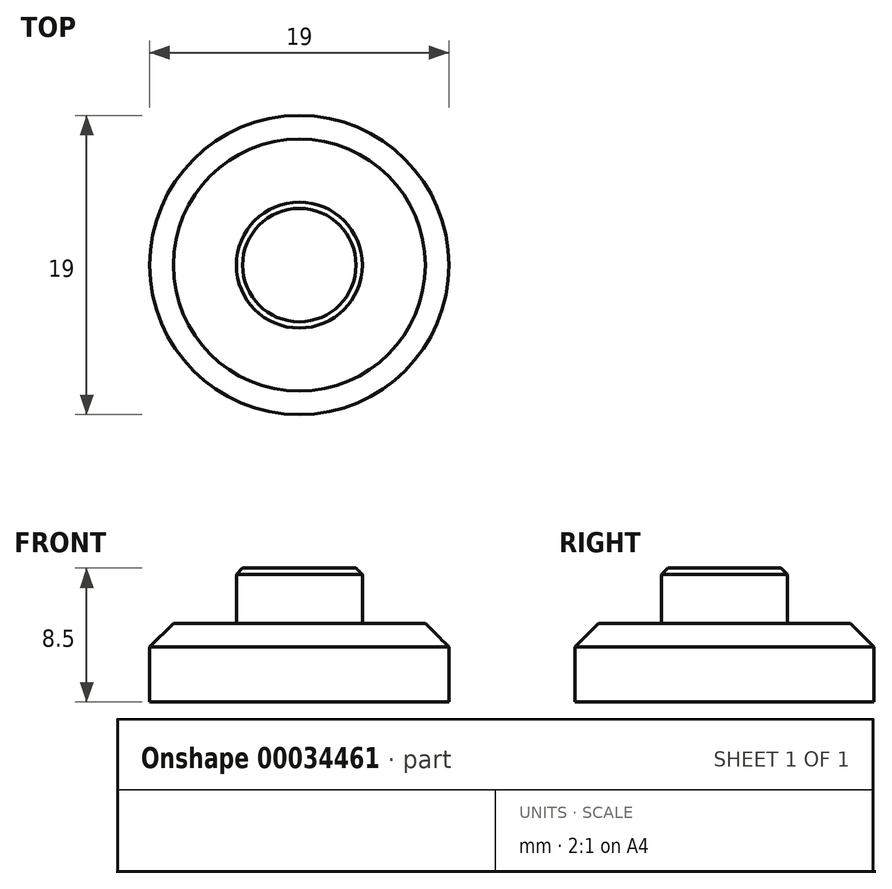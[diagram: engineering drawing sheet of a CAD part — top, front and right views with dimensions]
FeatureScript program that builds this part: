
annotation { "Feature Type Name" : "Feature", "Feature Type Description" : "" }
export const myFeature = defineFeature(function(context is Context, id is Id, definition is map)
    precondition{}
    {
        {
            var Q0;
            Q0=qCreatedBy(makeId("Top.planeOp"),FACE);
            var sketch = newSketch(context, id + "F0", { "sketchPlane" : qUnion([Q0])});
            skCircle(sketch, "E0", {"center": v(0, 0) * mm, "radius": 9.5 * mm});
            skSolve(sketch);
        }
        {
            var Q0;
            Q0 = qSketchRegion(id + "F0", true);
            extrude(context, id + "F1", {"entities" : qUnion([Q0]), "depth" : 5 * mm, "offsetDistance" : 25 * mm});
        }
        {
            var Q0;
            Q0=makeQuery(id+"F1.opExtrude","CAP_FACE",FACE,{"disambiguationData":[OSD([sQuery(id+"F0.wireOp",EDGE,"E0")])],"isStart":false});
            var sketch = newSketch(context, id + "F2", { "sketchPlane" : qUnion([Q0])});
            skCircle(sketch, "E1", {"center": v(0, 0) * mm, "radius": 4 * mm});
            skSolve(sketch);
        }
        {
            var Q0;
            Q0 = qSketchRegion(id + "F2", true);
            extrude(context, id + "F3", {"entities" : qUnion([Q0]), "operationType" : NewBodyOperationType.ADD, "depth" : 3.5 * mm, "offsetDistance" : 25 * mm});
        }
        {
            var Q0;
            Q0=makeQuery(id+"F1.opExtrude","CAP_EDGE",EDGE,{"disambiguationData":[OSD([sQuery(id+"F0.wireOp",EDGE,"E0")])],"isStart":false});
            chamfer(context, id + "F4", {"entities" : qUnion([Q0]), "width" : 1.5 * mm, "tangentPropagation" : true});
        }
        {
            var Q0;
            Q0=makeQuery(id+"F3.opExtrude","CAP_EDGE",EDGE,{"disambiguationData":[OSD([sQuery(id+"F2.wireOp",EDGE,"E1")])],"isStart":false});
            chamfer(context, id + "F5", {"entities" : qUnion([Q0]), "width" : 0.4 * mm, "tangentPropagation" : true});
        }
    });
